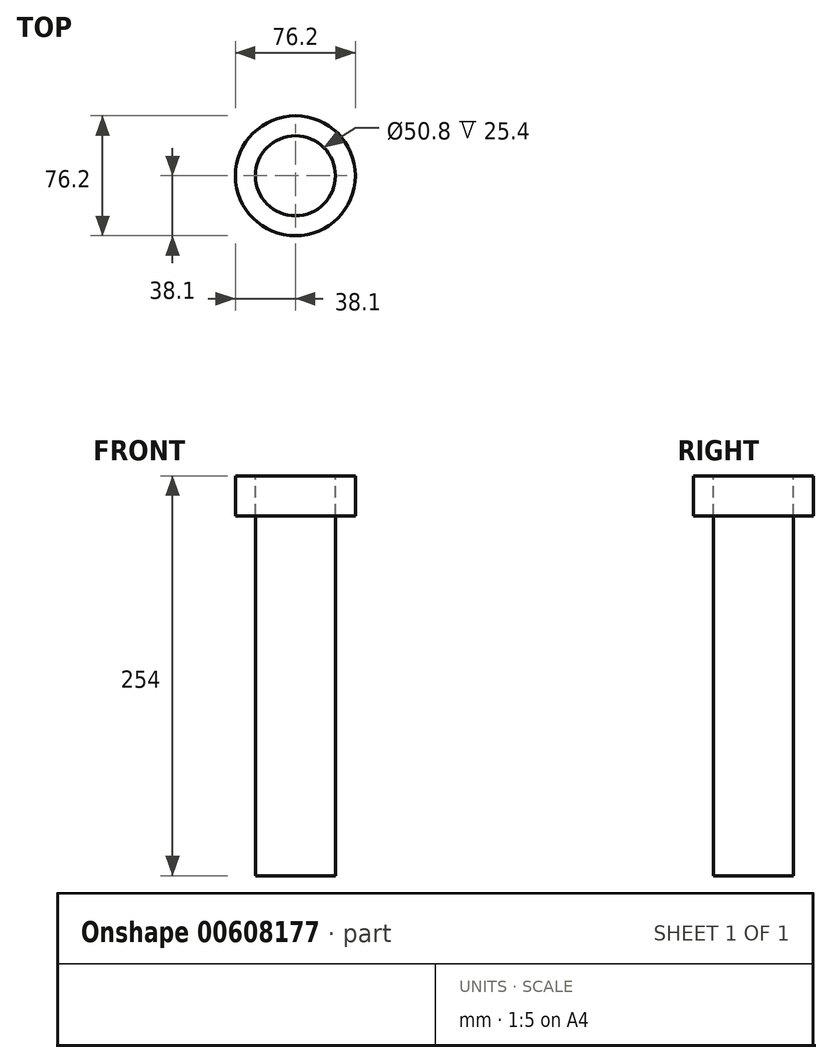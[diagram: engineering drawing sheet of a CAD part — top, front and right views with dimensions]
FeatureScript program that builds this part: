
annotation { "Feature Type Name" : "Feature", "Feature Type Description" : "" }
export const myFeature = defineFeature(function(context is Context, id is Id, definition is map)
    precondition{}
    {
        {
            var Q0;
            Q0=qCreatedBy(makeId("Top.planeOp"),FACE);
            var sketch = newSketch(context, id + "F0", { "sketchPlane" : qUnion([Q0])});
            skCircle(sketch, "E0", {"center": v(0, 0) * mm, "radius": 25.4 * mm});
            skSolve(sketch);
        }
        {
            var Q0;
            Q0=makeQuery(id+"F0.imprint","IMPRINT",FACE,{"disambiguationData":[TD([[makeQuery(id+"F0.imprint","IMPRINT",EDGE,{"derivedFrom":sQuery(id+"F0.wireOp",EDGE,"E0")}),1.0]])]});
            extrude(context, id + "F1", {"entities" : qUnion([Q0]), "depth" : 254 * mm, "offsetDistance" : 25.4 * mm});
        }
        {
            var Q0;
            Q0=makeQuery(id+"F1.opExtrude","CAP_FACE",FACE,{"disambiguationData":[OSD([sQuery(id+"F0.wireOp",EDGE,"E0")])],"isStart":false});
            var sketch = newSketch(context, id + "F2", { "sketchPlane" : qUnion([Q0])});
            skCircle(sketch, "E1", {"center": v(0, 0) * mm, "radius": 25.4 * mm});
            skCircle(sketch, "E2", {"center": v(0, 0) * mm, "radius": 38.1 * mm});
            skSolve(sketch);
        }
        {
            var Q0;
            Q0=makeQuery(id+"F2.imprint","IMPRINT",FACE,{"disambiguationData":[TD([[makeQuery(id+"F2.imprint","IMPRINT",EDGE,{"derivedFrom":sQuery(id+"F2.wireOp",EDGE,"E1")}),-1.0]])]});
            extrude(context, id + "F3", {"entities" : qUnion([Q0]), "oppositeDirection" : true, "depth" : 25.4 * mm, "offsetDistance" : 25.4 * mm});
        }
    });
